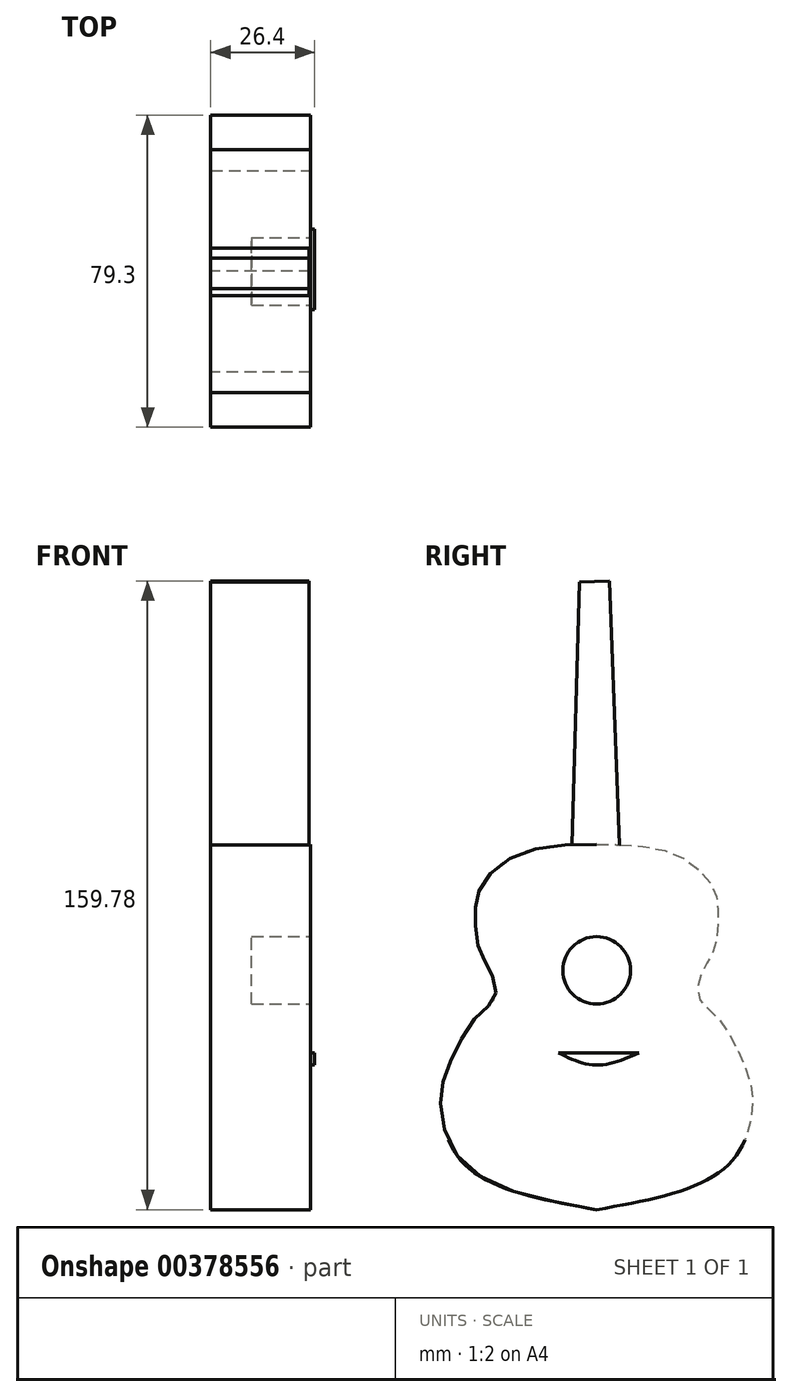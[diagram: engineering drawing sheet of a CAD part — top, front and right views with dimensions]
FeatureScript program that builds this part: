
annotation { "Feature Type Name" : "Feature", "Feature Type Description" : "" }
export const myFeature = defineFeature(function(context is Context, id is Id, definition is map)
    precondition{}
    {
        {
            var Q0;
            Q0=qCreatedBy(makeId("Right.planeOp"),FACE);
            var sketch = newSketch(context, id + "F0", { "sketchPlane" : qUnion([Q0])});
            skLineSegment(sketch, "E0", {"start": v(0, 32.01) * mm, "end": v(0, -60.8) * mm});
            skFitSpline(sketch, "E1", {"points": [v(0, 32.01) * mm, v(-20.26, 29.37) * mm, v(-29.66, 20.85) * mm, v(-30.84, 14.1) * mm, v(-29.96, 5.58) * mm, v(-27.02, 0) * mm, v(-25.85, -6.75) * mm, v(-30.25, -11.45) * mm, v(-37, -22.9) * mm, v(-39.65, -33.48) * mm, v(-33.19, -49.63) * mm, v(0, -60.8) * mm], "startDerivative": vector(-185.78, -1.8) * mm, "endDerivative": vector(256.11, -45.75) * mm});
            skFitSpline(sketch, "E2.MirrorCS", {"points": [v(0, 32.01) * mm, v(20.26, 29.37) * mm, v(29.66, 20.85) * mm, v(30.84, 14.1) * mm, v(29.96, 5.58) * mm, v(27.02, 0) * mm, v(25.85, -6.75) * mm, v(30.25, -11.45) * mm, v(37, -22.9) * mm, v(39.65, -33.48) * mm, v(33.19, -49.63) * mm, v(0, -60.8) * mm], "startDerivative": vector(185.78, -1.8) * mm, "endDerivative": vector(-256.11, -45.75) * mm});
            skSolve(sketch);
        }
        {
            var Q0;
            Q0=makeQuery(id+"F0.imprint","IMPRINT",FACE,{"disambiguationData":[TD([[makeQuery(id+"F0.imprint","IMPRINT",EDGE,{"derivedFrom":sQuery(id+"F0.wireOp",EDGE,"E0")}),-1.0]])]});
            var Q1;
            Q1=makeQuery(id+"F0.imprint","IMPRINT",FACE,{"disambiguationData":[TD([[makeQuery(id+"F0.imprint","IMPRINT",EDGE,{"derivedFrom":sQuery(id+"F0.wireOp",EDGE,"E0")}),1.0]])]});
            extrude(context, id + "F1", {"entities" : qUnion([Q0, Q1]), "depth" : 25.4 * mm});
        }
        {
            var Q0;
            Q0=makeQuery(id+"F1.opExtrude","CAP_FACE",FACE,{"disambiguationData":[OSD([sQuery(id+"F0.wireOp",EDGE,"E1"),sQuery(id+"F0.wireOp",EDGE,"E2.MirrorCS")])],"isStart":false});
            var sketch = newSketch(context, id + "F2", { "sketchPlane" : qUnion([Q0])});
            skCircle(sketch, "E3", {"center": v(0, 0) * mm, "radius": 8.58 * mm});
            skSolve(sketch);
        }
        {
            var Q0;
            Q0 = qSketchRegion(id + "F2", true);
            extrude(context, id + "F3", {"entities" : qUnion([Q0]), "operationType" : NewBodyOperationType.REMOVE, "oppositeDirection" : true, "depth" : 15 * mm});
        }
        {
            var Q0;
            Q0=makeQuery(id+"F1.opExtrude","CAP_FACE",FACE,{"disambiguationData":[OSD([sQuery(id+"F0.wireOp",EDGE,"E1"),sQuery(id+"F0.wireOp",EDGE,"E2.MirrorCS")])],"isStart":false});
            var sketch = newSketch(context, id + "F4", { "sketchPlane" : qUnion([Q0])});
            skCircle(sketch, "E4", {"center": v(0, 0) * mm, "radius": 10.3 * mm});
            skLineSegment(sketch, "E5", {"start": v(-2, 10.11) * mm, "end": v(-1.15, 8.5) * mm});
            skLineSegment(sketch, "E6", {"start": v(-1.15, 8.5) * mm, "end": v(-0.63, 10.29) * mm});
            skLineSegment(sketch, "E7", {"start": v(-0.63, 10.29) * mm, "end": v(0, 8.58) * mm});
            skLineSegment(sketch, "E8", {"start": v(0, 8.58) * mm, "end": v(0.5, 10.3) * mm});
            skLineSegment(sketch, "E9", {"start": v(0.5, 10.3) * mm, "end": v(1.18, 8.5) * mm});
            skLineSegment(sketch, "E10", {"start": v(1.18, 8.5) * mm, "end": v(1.66, 10.17) * mm});
            skLineSegment(sketch, "E11", {"start": v(1.66, 10.17) * mm, "end": v(2.5, 8.2) * mm});
            skLineSegment(sketch, "E12", {"start": v(2.5, 8.2) * mm, "end": v(3.62, 9.65) * mm});
            skLineSegment(sketch, "E13", {"start": v(3.62, 9.65) * mm, "end": v(3.62, 7.78) * mm});
            skLineSegment(sketch, "E14", {"start": v(3.62, 7.78) * mm, "end": v(5.3, 8.84) * mm});
            skLineSegment(sketch, "E15", {"start": v(5.3, 8.84) * mm, "end": v(5, 6.97) * mm});
            skLineSegment(sketch, "E16", {"start": v(5, 6.97) * mm, "end": v(6.85, 7.7) * mm});
            skLineSegment(sketch, "E17", {"start": v(6.85, 7.7) * mm, "end": v(6.3, 5.81) * mm});
            skLineSegment(sketch, "E18", {"start": v(6.3, 5.81) * mm, "end": v(8.09, 6.4) * mm});
            skLineSegment(sketch, "E19", {"start": v(8.09, 6.4) * mm, "end": v(7.12, 4.78) * mm});
            skLineSegment(sketch, "E20", {"start": v(7.12, 4.78) * mm, "end": v(9.13, 4.78) * mm});
            skLineSegment(sketch, "E21", {"start": v(9.13, 4.78) * mm, "end": v(7.81, 3.54) * mm});
            skLineSegment(sketch, "E22", {"start": v(7.81, 3.54) * mm, "end": v(9.68, 3.54) * mm});
            skLineSegment(sketch, "E23", {"start": v(9.68, 3.54) * mm, "end": v(8.28, 2.22) * mm});
            skLineSegment(sketch, "E24", {"start": v(8.28, 2.22) * mm, "end": v(10.17, 1.68) * mm});
            skLineSegment(sketch, "E25", {"start": v(10.17, 1.68) * mm, "end": v(8.53, 0.91) * mm});
            skLineSegment(sketch, "E26", {"start": v(8.53, 0.91) * mm, "end": v(10.3, 0.4) * mm});
            skLineSegment(sketch, "E27", {"start": v(10.3, 0.4) * mm, "end": v(8.56, -0.56) * mm});
            skLineSegment(sketch, "E28", {"start": v(8.56, -0.56) * mm, "end": v(10.2, -1.44) * mm});
            skLineSegment(sketch, "E29", {"start": v(10.2, -1.44) * mm, "end": v(8.34, -2) * mm});
            skLineSegment(sketch, "E30", {"start": v(8.34, -2) * mm, "end": v(9.83, -3.1) * mm});
            skLineSegment(sketch, "E31", {"start": v(9.83, -3.1) * mm, "end": v(8, -3.1) * mm});
            skLineSegment(sketch, "E32", {"start": v(8, -3.1) * mm, "end": v(9.28, -4.48) * mm});
            skLineSegment(sketch, "E33", {"start": v(9.28, -4.48) * mm, "end": v(7.32, -4.48) * mm});
            skLineSegment(sketch, "E34", {"start": v(7.32, -4.48) * mm, "end": v(8.37, -6.02) * mm});
            skLineSegment(sketch, "E35", {"start": v(8.37, -6.02) * mm, "end": v(6.58, -5.5) * mm});
            skLineSegment(sketch, "E36", {"start": v(6.58, -5.5) * mm, "end": v(7.3, -7.27) * mm});
            skLineSegment(sketch, "E37", {"start": v(7.3, -7.27) * mm, "end": v(5.64, -6.46) * mm});
            skLineSegment(sketch, "E38", {"start": v(5.64, -6.46) * mm, "end": v(6.1, -8.3) * mm});
            skLineSegment(sketch, "E39", {"start": v(6.1, -8.3) * mm, "end": v(4.55, -7.27) * mm});
            skLineSegment(sketch, "E40", {"start": v(4.55, -7.27) * mm, "end": v(4.9, -9.06) * mm});
            skLineSegment(sketch, "E41", {"start": v(4.9, -9.06) * mm, "end": v(3.22, -7.95) * mm});
            skLineSegment(sketch, "E42", {"start": v(3.22, -7.95) * mm, "end": v(3.22, -9.8) * mm});
            skLineSegment(sketch, "E43", {"start": v(3.22, -9.8) * mm, "end": v(1.88, -8.37) * mm});
            skLineSegment(sketch, "E44", {"start": v(1.88, -8.37) * mm, "end": v(1.88, -10.13) * mm});
            skLineSegment(sketch, "E45", {"start": v(1.88, -10.13) * mm, "end": v(0.5, -8.66) * mm});
            skLineSegment(sketch, "E46", {"start": v(0.5, -8.66) * mm, "end": v(0.5, -10.3) * mm});
            skLineSegment(sketch, "E47", {"start": v(0.5, -10.3) * mm, "end": v(-0.63, -8.55) * mm});
            skLineSegment(sketch, "E48", {"start": v(-0.63, -8.55) * mm, "end": v(-1.61, -10.18) * mm});
            skLineSegment(sketch, "E49", {"start": v(-1.61, -10.18) * mm, "end": v(-2.09, -8.32) * mm});
            skLineSegment(sketch, "E50", {"start": v(-2.09, -8.32) * mm, "end": v(-3.54, -9.68) * mm});
            skLineSegment(sketch, "E51", {"start": v(-3.54, -9.68) * mm, "end": v(-3.54, -7.81) * mm});
            skLineSegment(sketch, "E52", {"start": v(-3.54, -7.81) * mm, "end": v(-5.49, -8.72) * mm});
            skLineSegment(sketch, "E53", {"start": v(-5.49, -8.72) * mm, "end": v(-4.51, -7.3) * mm});
            skPoint(sketch, "E53.endSnap0", {"position": v(-4.51, -8.27) * mm});
            skLineSegment(sketch, "E54", {"start": v(-4.51, -7.3) * mm, "end": v(-6.33, -8.14) * mm});
            skLineSegment(sketch, "E55", {"start": v(-6.33, -8.14) * mm, "end": v(-6.33, -5.8) * mm});
            skLineSegment(sketch, "E56", {"start": v(-6.33, -5.8) * mm, "end": v(-7.96, -6.55) * mm});
            skLineSegment(sketch, "E57", {"start": v(-7.96, -6.55) * mm, "end": v(-7.34, -4.43) * mm});
            skLineSegment(sketch, "E58", {"start": v(-7.34, -4.43) * mm, "end": v(-8.92, -5.17) * mm});
            skLineSegment(sketch, "E59", {"start": v(-8.92, -5.17) * mm, "end": v(-7.83, -3.5) * mm});
            skLineSegment(sketch, "E60", {"start": v(-7.83, -3.5) * mm, "end": v(-9.9, -2.9) * mm});
            skLineSegment(sketch, "E61", {"start": v(-9.9, -2.9) * mm, "end": v(-8.44, -1.53) * mm});
            skLineSegment(sketch, "E62", {"start": v(-8.44, -1.53) * mm, "end": v(-10.26, -1) * mm});
            skLineSegment(sketch, "E63", {"start": v(-10.26, -1) * mm, "end": v(-8.57, -0.22) * mm});
            skLineSegment(sketch, "E64", {"start": v(-8.57, -0.22) * mm, "end": v(-10.27, 0.84) * mm});
            skLineSegment(sketch, "E65", {"start": v(-10.27, 0.84) * mm, "end": v(-8.4, 1.71) * mm});
            skLineSegment(sketch, "E66", {"start": v(-8.4, 1.71) * mm, "end": v(-9.8, 3.2) * mm});
            skLineSegment(sketch, "E67", {"start": v(-9.8, 3.2) * mm, "end": v(-7.96, 3.2) * mm});
            skLineSegment(sketch, "E68", {"start": v(-7.96, 3.2) * mm, "end": v(-8.9, 5.2) * mm});
            skLineSegment(sketch, "E69", {"start": v(-8.9, 5.2) * mm, "end": v(-6.82, 5.2) * mm});
            skLineSegment(sketch, "E70", {"start": v(-6.82, 5.2) * mm, "end": v(-7.62, 6.94) * mm});
            skLineSegment(sketch, "E71", {"start": v(-7.62, 6.94) * mm, "end": v(-5.72, 6.39) * mm});
            skLineSegment(sketch, "E72", {"start": v(-5.72, 6.39) * mm, "end": v(-6.48, 8.01) * mm});
            skLineSegment(sketch, "E73", {"start": v(-6.48, 8.01) * mm, "end": v(-4.35, 7.4) * mm});
            skLineSegment(sketch, "E74", {"start": v(-4.35, 7.4) * mm, "end": v(-4.76, 9.14) * mm});
            skLineSegment(sketch, "E75", {"start": v(-4.76, 9.14) * mm, "end": v(-3.03, 8.02) * mm});
            skLineSegment(sketch, "E76", {"start": v(-3.03, 8.02) * mm, "end": v(-3.03, 9.85) * mm});
            skLineSegment(sketch, "E77", {"start": v(-3.03, 9.85) * mm, "end": v(-2.3, 8.27) * mm});
            skLineSegment(sketch, "E78", {"start": v(-2.3, 8.27) * mm, "end": v(-2, 10.11) * mm});
            skSolve(sketch);
        }
        {
            var Q0;
            Q0=makeQuery(id+"F4.imprint","IMPRINT",FACE,{"disambiguationData":[TD([[makeQuery(id+"F4.imprint","IMPRINT",EDGE,{"derivedFrom":makeQuery(id+"F1.opExtrude","CAP_EDGE",EDGE,{"disambiguationData":[OSD([sQuery(id+"F0.wireOp",EDGE,"E1")])],"isStart":false})}),1.0]])]});
            var sketch = newSketch(context, id + "F5", { "sketchPlane" : qUnion([Q0])});
            skLineSegment(sketch, "E79", {"start": v(-9.71, -20.95) * mm, "end": v(10.7, -20.95) * mm});
            skFitSpline(sketch, "E80", {"points": [v(-9.71, -20.95) * mm, v(-4.72, -23.16) * mm, v(0, -24.05) * mm, v(5.26, -23.16) * mm, v(10.7, -20.95) * mm], "startDerivative": vector(19.83, -9.75) * mm, "endDerivative": vector(20.61, 9.38) * mm});
            skSolve(sketch);
        }
        {
            var Q0;
            Q0 = qSketchRegion(id + "F5", true);
            extrude(context, id + "F6", {"entities" : qUnion([Q0]), "operationType" : NewBodyOperationType.ADD, "depth" : 1 * mm});
        }
        {
            var Q0;
            Q0=makeQuery(id+"F1.opExtrude","CAP_FACE",FACE,{"disambiguationData":[OSD([sQuery(id+"F0.wireOp",EDGE,"E1"),sQuery(id+"F0.wireOp",EDGE,"E2.MirrorCS")])],"isStart":true});
            var sketch = newSketch(context, id + "F7", { "sketchPlane" : qUnion([Q0])});
            skLineSegment(sketch, "E81", {"start": v(-6.45, 15.82) * mm, "end": v(-3.3, 98.99) * mm});
            skLineSegment(sketch, "E82", {"start": v(-3.3, 98.99) * mm, "end": v(4.42, 98.7) * mm});
            skLineSegment(sketch, "E83", {"start": v(4.42, 98.7) * mm, "end": v(6.66, 16.08) * mm});
            skLineSegment(sketch, "E84", {"start": v(6.66, 16.08) * mm, "end": v(-6.45, 15.82) * mm});
            skSolve(sketch);
        }
        {
            var Q0;
            Q0 = qSketchRegion(id + "F7", true);
            extrude(context, id + "F8", {"entities" : qUnion([Q0]), "operationType" : NewBodyOperationType.ADD, "oppositeDirection" : true, "depth" : 25 * mm});
        }
    });
